# Revit family: LAMP_MUN LIGHT 480 SUSPENDED
name_source: partatom
category: Modelos genéricos
revit_build: Autodesk Revit 2015 (Build: 20140606_1530(x64)
units: mm (PartAtom-declared; Revit-internal decimal feet)

## types (8) — shared parameters
CRI = 80
Diameter = 480 mm  [stored 1.5748 ft]
Elevación por defecto = 1219 mm
Fabricante = LAMP
Gear = Electronic
Height = 64 mm  [stored 0.209974 ft]
IEE = A+
Installation instructions = https://www.lamp.es
Insulation class = I
LED Lifetime = 50.000 L80 B10
Last update = 11/11/2020
Luminaire type = Indoor - Downlight
MacAdam = <3
Manufacturer URL = http://www.lamp.es
Manufacturer country = Spain
Manufacturer name = LAMP
Photometric web file = Cuerpo Mun light 480 : 2181LM 3000 GRAPHITE
Power Supply = 220-240V 50-60Hz
Product URL = https://www.lamp.es
Product datasheet = http://www.lamp.es
Protection rating = IP20 / IK08
Weight = 6.00 kg

## per-type parameters (varying)
| type | Descripción | Efficacy | Finish | Initial color | Initial intensity | Lamp | Modelo | Plum | Power | Product code | Type |
| 2181LM 4000 GRAPHITE | MUN LIGHT SUS Ø480 2500 NW GRH. | 94 lm/W | Texturised matte graphite | 4000 K | 2181 lm | LOW POWER LED | ML1480SU25840NB | 23 W | 20 W | ML1480SU25840NB | LOW POWER OSRAM |
| 2181LM 3000 GRAPHITE | MUN LIGHT SUS Ø480 2500 WW GRH. | 94 lm/W | Texturised matte graphite | 3000 K | 2181 lm | LOW POWER LED | ML1480SU25830NB | 23 W | 20 W | ML1480SU25830NB | LOW POWER OSRAM |
| 2311LM 4000 WHITE | MUN LIGHT SUS Ø480 2500 NW WH. | 100 lm/W | Texturised matte white | 4000 K | 2311 lm | LOW POWER LED | ML1480SU25840NW | 23 W | 20 W | ML1480SU25840NW | LOW POWER OSRAM |
| 2311LM 3000 WHITE | MUN LIGHT SUS Ø480 2500 WW WH. | 100 lm/W | Texturised matte white | 3000 K | 2311 lm | LOW POWER LED | ML1480SU25830NW | 23 W | 20 W | ML1480SU25830NW | LOW POWER OSRAM |
| 4317LM 4000 GRAPHITE | MUN LIGHT SUS Ø480 4000 NW GRH. | 70 lm/W | Texturised matte graphite | 4000 K | 4317 lm | MID-POWER LED | ML1480SU40840NB | 62 W | 59 W | ML1480SU40840NB | MID POWER OSRAM |
| 4317LM 3000 GRAPHITE | MUN LIGHT SUS Ø480 4000 WW GRH. | 70 lm/W | Texturised matte graphite | 3000 K | 4317 lm | MID-POWER LED | ML1480SU40830NB | 62 W | 59 W | ML1480SU40830NB | MID POWER OSRAM |
| 4576LM 4000 WHITE | MUN LIGHT SUS Ø480 4000 NW WH. | 74 lm/W | Texturised matte white | 4000 K | 4576 lm | MID-POWER LED | ML1480SU40840NW | 62 W | 59 W | ML1480SU40840NW | MID POWER OSRAM |
| 4576LM 3000 WHITE | MUN LIGHT SUS Ø480 4000 WW WH. | 74 lm/W | Texturised matte white | 3000 K | 4576 lm | MID-POWER LED | ML1480SU40830NW | 62 W | 59 W | ML1480SU40830NW | MID POWER OSRAM |

note: [stored X ft] marks values corroborated as IEEE doubles in the binary element streams (Revit-internal decimal feet)
